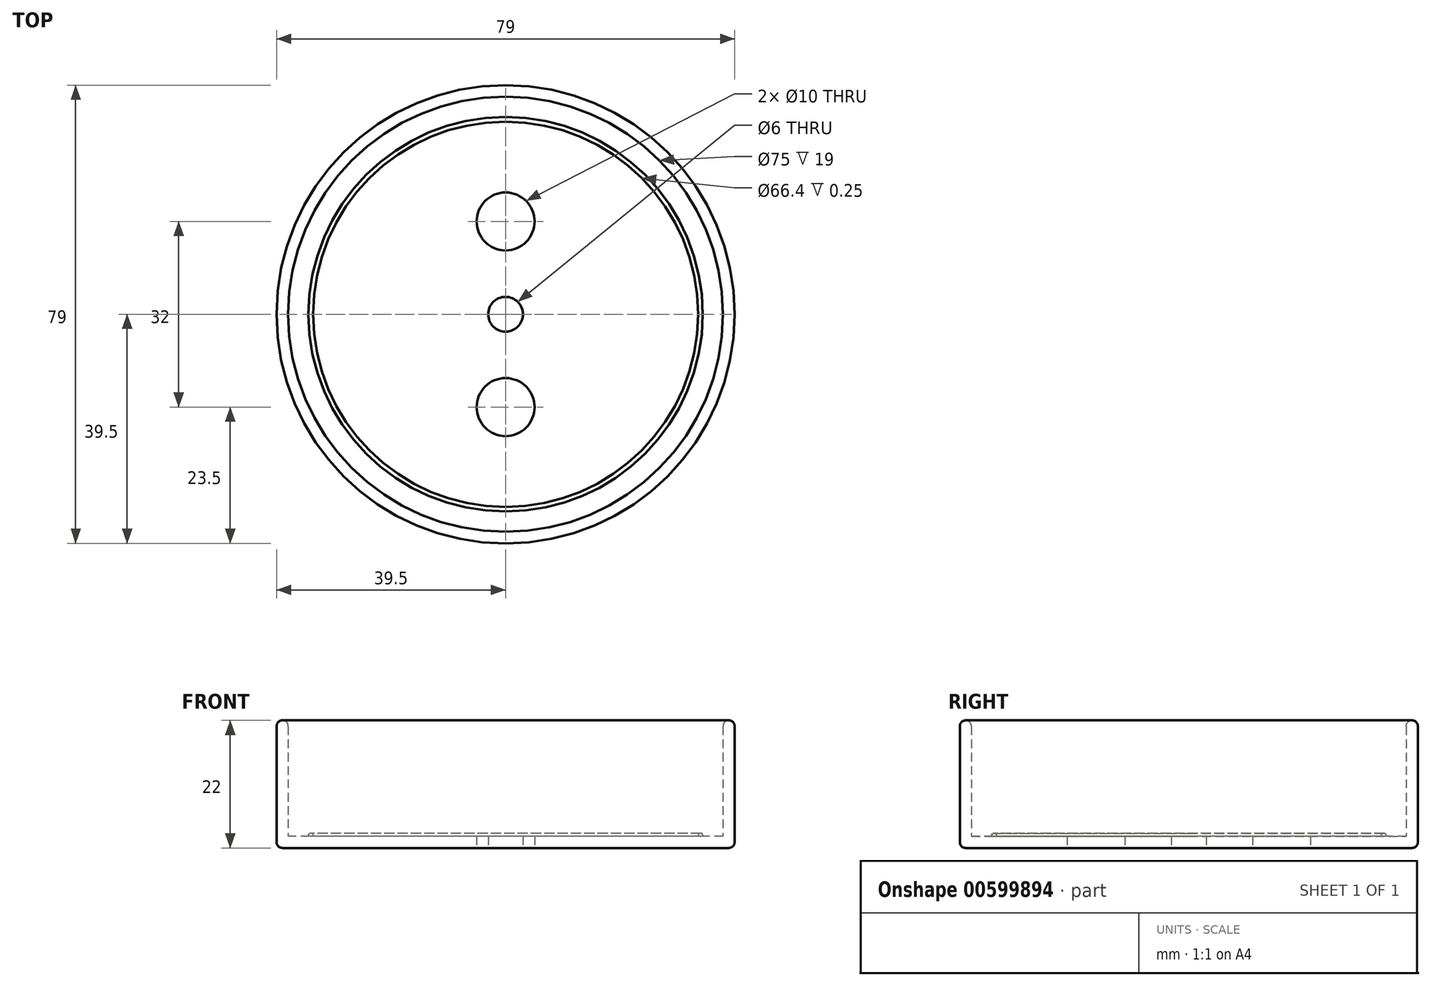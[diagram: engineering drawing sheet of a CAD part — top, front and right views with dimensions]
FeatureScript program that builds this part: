
annotation { "Feature Type Name" : "Feature", "Feature Type Description" : "" }
export const myFeature = defineFeature(function(context is Context, id is Id, definition is map)
    precondition{}
    {
        {
            var Q0;
            Q0=qCreatedBy(makeId("Top.planeOp"),FACE);
            var sketch = newSketch(context, id + "F0", { "sketchPlane" : qUnion([Q0])});
            skCircle(sketch, "E0", {"center": v(0, 0) * mm, "radius": 37.5 * mm});
            skCircle(sketch, "E1", {"center": v(0, 0) * mm, "radius": 39.5 * mm});
            skCircle(sketch, "E2", {"center": v(0, 0) * mm, "radius": 3 * mm});
            skCircle(sketch, "E3", {"center": v(0, 16) * mm, "radius": 5 * mm});
            skCircle(sketch, "E4", {"center": v(0, -16) * mm, "radius": 5 * mm});
            skSolve(sketch);
        }
        {
            var Q0;
            Q0=makeQuery(id+"F0.imprint","IMPRINT",FACE,{"disambiguationData":[TD([[makeQuery(id+"F0.imprint","IMPRINT",EDGE,{"derivedFrom":sQuery(id+"F0.wireOp",EDGE,"E0")}),1.0]])]});
            extrude(context, id + "F1", {"entities" : qUnion([Q0]), "depth" : 2 * mm, "offsetDistance" : 25 * mm});
        }
        {
            var Q0;
            Q0=makeQuery(id+"F0.imprint","IMPRINT",FACE,{"disambiguationData":[TD([[makeQuery(id+"F0.imprint","IMPRINT",EDGE,{"derivedFrom":sQuery(id+"F0.wireOp",EDGE,"E0")}),-1.0]])]});
            extrude(context, id + "F2", {"entities" : qUnion([Q0]), "operationType" : NewBodyOperationType.ADD, "depth" : 22 * mm, "offsetDistance" : 25 * mm});
        }
        {
            var Q0;
            Q0=makeQuery(id+"F1.opExtrude","CAP_FACE",FACE,{"disambiguationData":[OSD([sQuery(id+"F0.wireOp",EDGE,"E0"),sQuery(id+"F0.wireOp",EDGE,"E2"),sQuery(id+"F0.wireOp",EDGE,"E3"),sQuery(id+"F0.wireOp",EDGE,"E4")])],"isStart":false});
            var sketch = newSketch(context, id + "F3", { "sketchPlane" : qUnion([Q0])});
            skCircle(sketch, "E5", {"center": v(0, 0) * mm, "radius": 34 * mm});
            skCircle(sketch, "E6", {"center": v(0, 0) * mm, "radius": 33.2 * mm});
            skSolve(sketch);
        }
        {
            var Q0;
            Q0 = qSketchRegion(id + "F3", true);
            extrude(context, id + "F4", {"entities" : qUnion([Q0]), "operationType" : NewBodyOperationType.ADD, "depth" : .5 * mm, "offsetDistance" : 25 * mm});
        }
        {
            var Q0;
            Q0=makeQuery(id+"F4.opExtrude","CAP_FACE",FACE,{"disambiguationData":[OSD([sQuery(id+"F3.wireOp",EDGE,"E5"),sQuery(id+"F3.wireOp",EDGE,"E6")])],"isStart":false});
            var Q1;
            Q1=makeQuery(id+"F4.opExtrude","CAP_EDGE",EDGE,{"disambiguationData":[OSD([sQuery(id+"F3.wireOp",EDGE,"E6")])],"isStart":true});
            var Q2;
            Q2=makeQuery(id+"F4.opExtrude","CAP_EDGE",EDGE,{"disambiguationData":[OSD([sQuery(id+"F3.wireOp",EDGE,"E5")])],"isStart":true});
            fillet(context, id + "F5", {"entities" : qUnion([Q0, Q1, Q2]), "radius" : .25 * mm, "tangentPropagation" : true, "allowEdgeOverflow" : false});
        }
        {
            var Q0;
            Q0=makeQuery(id+"F1.opExtrude","CAP_EDGE",EDGE,{"disambiguationData":[OSD([sQuery(id+"F0.wireOp",EDGE,"E0")])],"isStart":false});
            var Q1;
            Q1=makeQuery(id+"F2.opExtrude","CAP_EDGE",EDGE,{"disambiguationData":[OSD([sQuery(id+"F0.wireOp",EDGE,"E1")])],"isStart":true});
            var Q2;
            Q2=makeQuery(id+"F2.opExtrude","CAP_FACE",FACE,{"disambiguationData":[OSD([sQuery(id+"F0.wireOp",EDGE,"E0"),sQuery(id+"F0.wireOp",EDGE,"E1")])],"isStart":false});
            fillet(context, id + "F6", {"entities" : qUnion([Q0, Q1, Q2]), "radius" : 1 * mm, "tangentPropagation" : true, "allowEdgeOverflow" : false});
        }
    });
